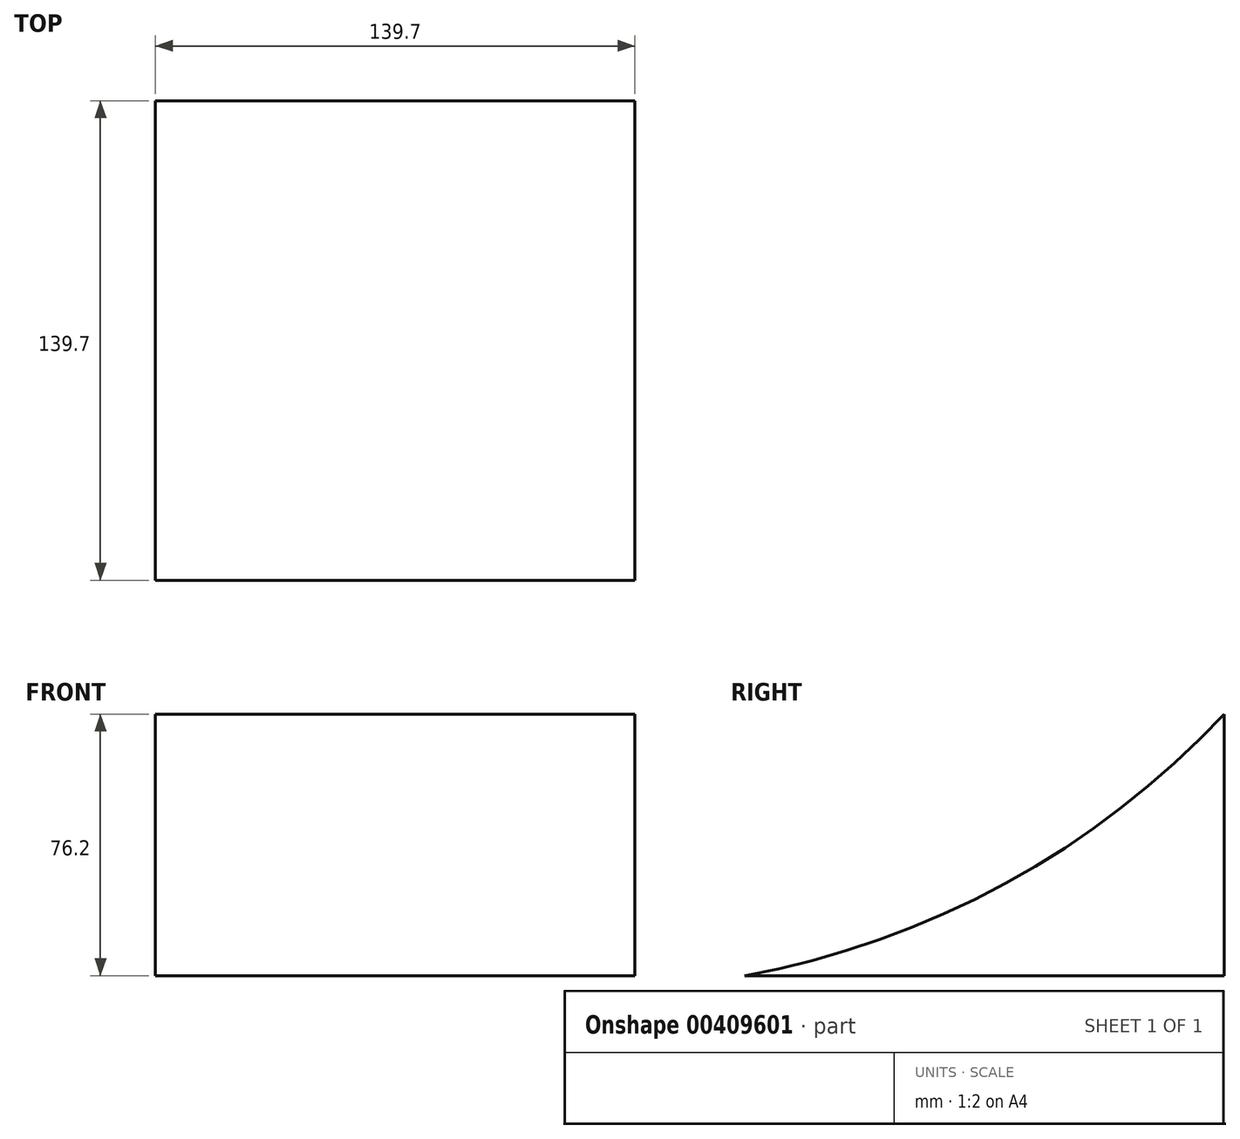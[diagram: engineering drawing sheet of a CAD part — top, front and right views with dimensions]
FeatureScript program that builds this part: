
annotation { "Feature Type Name" : "Feature", "Feature Type Description" : "" }
export const myFeature = defineFeature(function(context is Context, id is Id, definition is map)
    precondition{}
    {
        {
            var Q0;
            Q0=qCreatedBy(makeId("Top.planeOp"),FACE);
            var sketch = newSketch(context, id + "F0", { "sketchPlane" : qUnion([Q0])});
            skLineSegment(sketch, "E0.bottom", {"start": v(69.85, 69.85) * mm, "end": v(-69.85, 69.85) * mm});
            skLineSegment(sketch, "E0.top", {"start": v(69.85, -69.85) * mm, "end": v(-69.85, -69.85) * mm});
            skLineSegment(sketch, "E0.left", {"start": v(69.85, 69.85) * mm, "end": v(69.85, -69.85) * mm});
            skLineSegment(sketch, "E0.right", {"start": v(-69.85, 69.85) * mm, "end": v(-69.85, -69.85) * mm});
            skPoint(sketch, "E0.middle", {"position": v(0, 0) * mm});
            skSolve(sketch);
        }
        {
            var Q0;
            Q0 = qSketchRegion(id + "F0", true);
            extrude(context, id + "F1", {"entities" : qUnion([Q0]), "depth" : 76.2 * mm});
        }
        {
            var Q0;
            Q0=makeQuery(id+"F1.opExtrude","SWEPT_FACE",FACE,{"disambiguationData":[OSD([sQuery(id+"F0.wireOp",EDGE,"E0.left")])]});
            var sketch = newSketch(context, id + "F2", { "sketchPlane" : qUnion([Q0])});
            skArc(sketch, "E1", {"start": v(-69.85, 0) * mm, "mid": v(6.12, 26.88) * mm, "end": v(69.85, 76.2) * mm});
            skLineSegment(sketch, "E2", {"start": v(-69.85, 0) * mm, "end": v(-69.85, 76.2) * mm});
            skLineSegment(sketch, "E3", {"start": v(-69.85, 76.2) * mm, "end": v(69.85, 76.2) * mm});
            skSolve(sketch);
        }
        {
            var Q0;
            Q0 = qSketchRegion(id + "F2", true);
            extrude(context, id + "F3", {"entities" : qUnion([Q0]), "operationType" : NewBodyOperationType.REMOVE, "endBound" : BoundingType.THROUGH_ALL, "oppositeDirection" : true, "depth" : 25.4 * mm});
        }
    });
